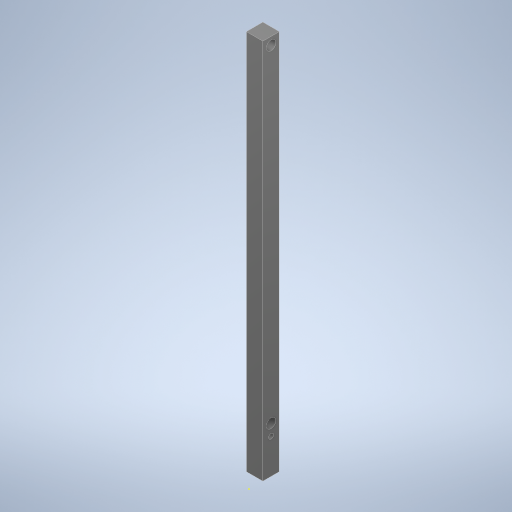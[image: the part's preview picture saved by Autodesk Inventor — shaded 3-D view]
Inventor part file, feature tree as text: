
AUTODESK INVENTOR PART (.ipt)
format: ipt  version: 2024 (Build 280153000, 153)  size: 774,144 bytes
history: native  units: in
note: dims shown in document units (in); Inventor stores cm internally (conversion verified against a paired STEP export)
features: sketch x5, hole x2, extrude x2, imported_body x1
ambient origin geometry x8: Origin, YZ Plane, XZ Plane, XY Plane, X Axis, Y Axis, Z Axis, Center Point
bodies: Solid1 (feature_tree)
feature tree (10):
  imported_body  "Base1"
  hole  "Hole1"  [1 undecoded]
  sketch  "Sketch2"  dims[d2=0.0625in d3=0.75in d4=0.375in d5=0.25in d6=0.5635in d7=1.0in d8=0.8108in d9=0.208in d10=0.0in]
  extrude  "Extrusion1"  Depth=0.208in TaperAngle=0.0deg
  extrude  "Extrusion2"  Depth=0.0984in
  hole  "Hole2"  [1 undecoded]
  sketch  "Sketch1"  dims[d0=0.407in d1=0.0312in]
  sketch  "Sketch3"  dims[d11=0.483in d12=0.0in d13=0.0984in]
  sketch  "Sketch4"  dims[d14=4.2323in d15=0.12in]
  sketch  "Sketch5"  dims[d16=0.12in d17=0.12in d18=0.75in d19=0.375in d20=0.25in d21=0.5635in d22=1.0in d23=0.8108in d24=0.75in d25=0.8108in d26=0.0625in d27=0.75in d28=0.375in]
note: 2 required parameter values undecoded (feature->parameter linkage not recoverable at this tier; creation-order binding heuristic only, values carry confidence <= 0.55)
